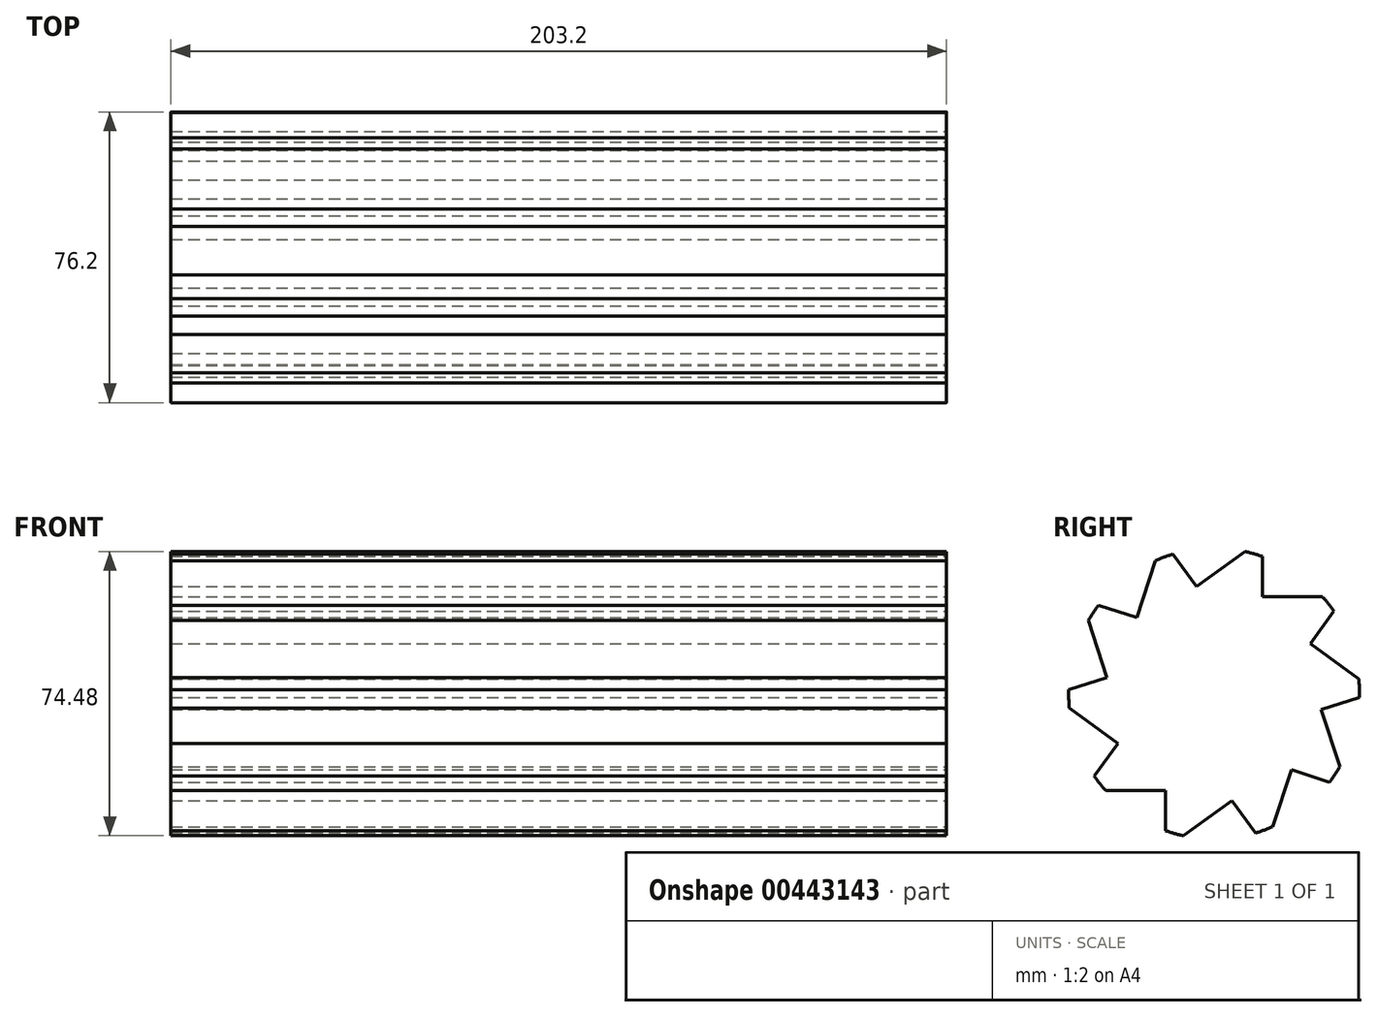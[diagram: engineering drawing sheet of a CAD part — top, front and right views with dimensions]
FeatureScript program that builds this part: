
annotation { "Feature Type Name" : "Feature", "Feature Type Description" : "" }
export const myFeature = defineFeature(function(context is Context, id is Id, definition is map)
    precondition{}
    {
        {
            var Q0;
            Q0=qCreatedBy(makeId("Right.planeOp"),FACE);
            var sketch = newSketch(context, id + "F0", { "sketchPlane" : qUnion([Q0])});
            skCircle(sketch, "E0", {"center": v(0, 0) * mm, "radius": 38.1 * mm});
            skSolve(sketch);
        }
        {
            var Q0;
            Q0=makeQuery(id+"F0.imprint","IMPRINT",FACE,{"disambiguationData":[TD([[makeQuery(id+"F0.imprint","IMPRINT",EDGE,{"derivedFrom":sQuery(id+"F0.wireOp",EDGE,"E0")}),1.0]])]});
            extrude(context, id + "F1", {"entities" : qUnion([Q0]), "depth" : 203.2 * mm});
        }
        {
            var Q0;
            Q0=makeQuery(id+"F1.opExtrude","CAP_FACE",FACE,{"disambiguationData":[OSD([sQuery(id+"F0.wireOp",EDGE,"E0")])],"isStart":false});
            var sketch = newSketch(context, id + "F2", { "sketchPlane" : qUnion([Q0])});
            skLineSegment(sketch, "E1.bottom", {"start": v(12.7, 25.4) * mm, "end": v(35.56, 25.4) * mm});
            skLineSegment(sketch, "E1.top", {"start": v(12.7, 50.8) * mm, "end": v(35.56, 50.8) * mm});
            skLineSegment(sketch, "E1.left", {"start": v(12.7, 25.4) * mm, "end": v(12.7, 50.8) * mm});
            skLineSegment(sketch, "E1.right", {"start": v(35.56, 25.4) * mm, "end": v(35.56, 50.8) * mm});
            skLineSegment(sketch, "E2.1.0", {"start": v(-19.58, 48.56) * mm, "end": v(-1.1, 62) * mm});
            skLineSegment(sketch, "E2.1.1", {"start": v(13.84, 41.45) * mm, "end": v(-1.1, 62) * mm});
            skLineSegment(sketch, "E2.1.2", {"start": v(-4.66, 28.01) * mm, "end": v(13.84, 41.45) * mm});
            skLineSegment(sketch, "E2.1.3", {"start": v(-4.66, 28.01) * mm, "end": v(-19.58, 48.56) * mm});
            skLineSegment(sketch, "E2.2.0", {"start": v(-44.39, 27.78) * mm, "end": v(-37.33, 49.52) * mm});
            skLineSegment(sketch, "E2.2.1", {"start": v(-13.17, 41.67) * mm, "end": v(-37.33, 49.52) * mm});
            skLineSegment(sketch, "E2.2.2", {"start": v(-20.23, 19.93) * mm, "end": v(-13.17, 41.67) * mm});
            skLineSegment(sketch, "E2.2.3", {"start": v(-20.23, 19.93) * mm, "end": v(-44.39, 27.78) * mm});
            skPoint(sketch, "E2.center", {"position": v(0, 0) * mm});
            skLineSegment(sketch, "E3.1.3.0", {"start": v(-52.24, -3.62) * mm, "end": v(-59.3, 18.12) * mm});
            skLineSegment(sketch, "E3.3.3.0", {"start": v(-35.15, 25.97) * mm, "end": v(-59.3, 18.12) * mm});
            skLineSegment(sketch, "E3.6.3.0", {"start": v(-28.08, 4.23) * mm, "end": v(-35.15, 25.97) * mm});
            skLineSegment(sketch, "E3.9.3.0", {"start": v(-28.08, 4.23) * mm, "end": v(-52.24, -3.62) * mm});
            skLineSegment(sketch, "E3.1.4.0", {"start": v(-40.13, -33.63) * mm, "end": v(-58.63, -20.2) * mm});
            skLineSegment(sketch, "E3.3.4.0", {"start": v(-43.7, 0.35) * mm, "end": v(-58.63, -20.2) * mm});
            skLineSegment(sketch, "E3.6.4.0", {"start": v(-25.2, -13.08) * mm, "end": v(-43.7, 0.35) * mm});
            skLineSegment(sketch, "E3.9.4.0", {"start": v(-25.2, -13.08) * mm, "end": v(-40.13, -33.63) * mm});
            skLineSegment(sketch, "E3.1.5.0", {"start": v(-12.7, -50.8) * mm, "end": v(-35.56, -50.8) * mm});
            skLineSegment(sketch, "E3.3.5.0", {"start": v(-35.56, -25.4) * mm, "end": v(-35.56, -50.8) * mm});
            skLineSegment(sketch, "E3.6.5.0", {"start": v(-12.7, -25.4) * mm, "end": v(-35.56, -25.4) * mm});
            skLineSegment(sketch, "E3.9.5.0", {"start": v(-12.7, -25.4) * mm, "end": v(-12.7, -50.8) * mm});
            skLineSegment(sketch, "E3.1.6.0", {"start": v(19.58, -48.56) * mm, "end": v(1.1, -62) * mm});
            skLineSegment(sketch, "E3.3.6.0", {"start": v(-13.84, -41.45) * mm, "end": v(1.1, -62) * mm});
            skLineSegment(sketch, "E3.6.6.0", {"start": v(4.66, -28.01) * mm, "end": v(-13.84, -41.45) * mm});
            skLineSegment(sketch, "E3.9.6.0", {"start": v(4.66, -28.01) * mm, "end": v(19.58, -48.56) * mm});
            skLineSegment(sketch, "E3.1.7.0", {"start": v(44.39, -27.78) * mm, "end": v(37.33, -49.52) * mm});
            skLineSegment(sketch, "E3.3.7.0", {"start": v(13.17, -41.67) * mm, "end": v(37.33, -49.52) * mm});
            skLineSegment(sketch, "E3.6.7.0", {"start": v(20.23, -19.93) * mm, "end": v(13.17, -41.67) * mm});
            skLineSegment(sketch, "E3.9.7.0", {"start": v(20.23, -19.93) * mm, "end": v(44.39, -27.78) * mm});
            skLineSegment(sketch, "E3.1.8.0", {"start": v(52.24, 3.62) * mm, "end": v(59.3, -18.12) * mm});
            skLineSegment(sketch, "E3.3.8.0", {"start": v(35.15, -25.97) * mm, "end": v(59.3, -18.12) * mm});
            skLineSegment(sketch, "E3.6.8.0", {"start": v(28.08, -4.23) * mm, "end": v(35.15, -25.97) * mm});
            skLineSegment(sketch, "E3.9.8.0", {"start": v(28.08, -4.23) * mm, "end": v(52.24, 3.62) * mm});
            skLineSegment(sketch, "E3.1.9.0", {"start": v(40.13, 33.63) * mm, "end": v(58.63, 20.2) * mm});
            skLineSegment(sketch, "E3.3.9.0", {"start": v(43.7, -0.35) * mm, "end": v(58.63, 20.2) * mm});
            skLineSegment(sketch, "E3.6.9.0", {"start": v(25.2, 13.08) * mm, "end": v(43.7, -0.35) * mm});
            skLineSegment(sketch, "E3.9.9.0", {"start": v(25.2, 13.08) * mm, "end": v(40.13, 33.63) * mm});
            skSolve(sketch);
        }
        {
            var Q0;
            {var subQ0=sQuery(id+"F2.wireOp",EDGE,"E1.left");var subQ1=sQuery(id+"F2.wireOp",EDGE,"E1.bottom");var subQ2=makeQuery(id+"F2.imprint","INTERSECT",VERTEX,{"derivedFrom":[subQ1,subQ0]});Q0=makeQuery(id+"F2.imprint","IMPRINT",FACE,{"disambiguationData":[TD([[makeQuery(id+"F2.imprint","IMPRINT",EDGE,{"disambiguationData":[TD([[subQ2,-1.0]])],"derivedFrom":subQ1}),1.0]])]});}
            var Q1;
            {var subQ0=sQuery(id+"F2.wireOp",EDGE,"E3.9.9.0");var subQ1=sQuery(id+"F2.wireOp",EDGE,"E3.6.9.0");var subQ2=makeQuery(id+"F2.imprint","INTERSECT",VERTEX,{"derivedFrom":[subQ1,subQ0]});Q1=makeQuery(id+"F2.imprint","IMPRINT",FACE,{"disambiguationData":[TD([[makeQuery(id+"F2.imprint","IMPRINT",EDGE,{"disambiguationData":[TD([[subQ2,-1.0]])],"derivedFrom":subQ1}),1.0]])]});}
            var Q2;
            {var subQ0=sQuery(id+"F2.wireOp",EDGE,"E3.9.8.0");var subQ1=sQuery(id+"F2.wireOp",EDGE,"E3.6.8.0");var subQ2=makeQuery(id+"F2.imprint","INTERSECT",VERTEX,{"derivedFrom":[subQ1,subQ0]});Q2=makeQuery(id+"F2.imprint","IMPRINT",FACE,{"disambiguationData":[TD([[makeQuery(id+"F2.imprint","IMPRINT",EDGE,{"disambiguationData":[TD([[subQ2,-1.0]])],"derivedFrom":subQ1}),1.0]])]});}
            var Q3;
            {var subQ0=sQuery(id+"F2.wireOp",EDGE,"E3.9.7.0");var subQ1=sQuery(id+"F2.wireOp",EDGE,"E3.6.7.0");var subQ2=makeQuery(id+"F2.imprint","INTERSECT",VERTEX,{"derivedFrom":[subQ1,subQ0]});Q3=makeQuery(id+"F2.imprint","IMPRINT",FACE,{"disambiguationData":[TD([[makeQuery(id+"F2.imprint","IMPRINT",EDGE,{"disambiguationData":[TD([[subQ2,-1.0]])],"derivedFrom":subQ1}),1.0]])]});}
            var Q4;
            {var subQ0=sQuery(id+"F2.wireOp",EDGE,"E2.1.3");var subQ1=sQuery(id+"F2.wireOp",EDGE,"E2.1.2");var subQ2=makeQuery(id+"F2.imprint","INTERSECT",VERTEX,{"derivedFrom":[subQ1,subQ0]});Q4=makeQuery(id+"F2.imprint","IMPRINT",FACE,{"disambiguationData":[TD([[makeQuery(id+"F2.imprint","IMPRINT",EDGE,{"disambiguationData":[TD([[subQ2,-1.0]])],"derivedFrom":subQ1}),1.0]])]});}
            var Q5;
            {var subQ0=sQuery(id+"F2.wireOp",EDGE,"E3.9.4.0");var subQ1=sQuery(id+"F2.wireOp",EDGE,"E3.6.4.0");var subQ2=makeQuery(id+"F2.imprint","INTERSECT",VERTEX,{"derivedFrom":[subQ1,subQ0]});Q5=makeQuery(id+"F2.imprint","IMPRINT",FACE,{"disambiguationData":[TD([[makeQuery(id+"F2.imprint","IMPRINT",EDGE,{"disambiguationData":[TD([[subQ2,-1.0]])],"derivedFrom":subQ1}),1.0]])]});}
            var Q6;
            {var subQ0=sQuery(id+"F2.wireOp",EDGE,"E3.9.5.0");var subQ1=sQuery(id+"F2.wireOp",EDGE,"E3.6.5.0");var subQ2=makeQuery(id+"F2.imprint","INTERSECT",VERTEX,{"derivedFrom":[subQ1,subQ0]});Q6=makeQuery(id+"F2.imprint","IMPRINT",FACE,{"disambiguationData":[TD([[makeQuery(id+"F2.imprint","IMPRINT",EDGE,{"disambiguationData":[TD([[subQ2,-1.0]])],"derivedFrom":subQ1}),1.0]])]});}
            var Q7;
            {var subQ0=sQuery(id+"F2.wireOp",EDGE,"E3.9.6.0");var subQ1=sQuery(id+"F2.wireOp",EDGE,"E3.6.6.0");var subQ2=makeQuery(id+"F2.imprint","INTERSECT",VERTEX,{"derivedFrom":[subQ1,subQ0]});Q7=makeQuery(id+"F2.imprint","IMPRINT",FACE,{"disambiguationData":[TD([[makeQuery(id+"F2.imprint","IMPRINT",EDGE,{"disambiguationData":[TD([[subQ2,-1.0]])],"derivedFrom":subQ1}),1.0]])]});}
            var Q8;
            {var subQ0=sQuery(id+"F2.wireOp",EDGE,"E3.9.3.0");var subQ1=sQuery(id+"F2.wireOp",EDGE,"E3.6.3.0");var subQ2=makeQuery(id+"F2.imprint","INTERSECT",VERTEX,{"derivedFrom":[subQ1,subQ0]});Q8=makeQuery(id+"F2.imprint","IMPRINT",FACE,{"disambiguationData":[TD([[makeQuery(id+"F2.imprint","IMPRINT",EDGE,{"disambiguationData":[TD([[subQ2,-1.0]])],"derivedFrom":subQ1}),1.0]])]});}
            var Q9;
            {var subQ0=sQuery(id+"F2.wireOp",EDGE,"E2.2.3");var subQ1=sQuery(id+"F2.wireOp",EDGE,"E2.2.2");var subQ2=makeQuery(id+"F2.imprint","INTERSECT",VERTEX,{"derivedFrom":[subQ1,subQ0]});Q9=makeQuery(id+"F2.imprint","IMPRINT",FACE,{"disambiguationData":[TD([[makeQuery(id+"F2.imprint","IMPRINT",EDGE,{"disambiguationData":[TD([[subQ2,-1.0]])],"derivedFrom":subQ1}),1.0]])]});}
            extrude(context, id + "F3", {"entities" : qUnion([Q0, Q1, Q2, Q3, Q4, Q5, Q6, Q7, Q8, Q9]), "operationType" : NewBodyOperationType.REMOVE, "oppositeDirection" : true, "depth" : 228.6 * mm});
        }
    });
